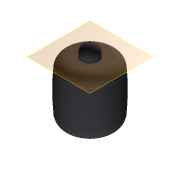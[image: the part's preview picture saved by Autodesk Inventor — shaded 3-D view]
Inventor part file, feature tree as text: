
AUTODESK INVENTOR PART (.ipt)
format: ipt  version: 2017 (Build 210142000, 142)  size: 145,408 bytes
history: native  units: mm
features: sketch x3, fillet x3, mirror x2, plane x1, loft x1, extrude x1
ambient origin geometry x8: Origin, YZ Plane, XZ Plane, XY Plane, X Axis, Y Axis, Z Axis, Center Point
bodies: Solid1 (feature_tree)
feature tree (11):
  sketch  "Sketch1"  dims[d0=12.0mm d1=6.0mm d2=10.5mm d3=0.0mm d4=90.0deg]
  plane  "Work Plane1"
  loft  "Loft1"
  mirror  "Mirror1"
  fillet  "Fillet1"  Radius=10.5mm
  fillet  "Fillet2"  [1 undecoded]
  extrude  "Extrusion1"  Depth=50.0mm
  fillet  "Fillet3"  Radius=2.0mm
  mirror  "Mirror2"
  sketch  "Sketch2"  dims[d5=0.0mm d6=90.0deg d7=50.0mm d8=2.0mm]
  sketch  "Sketch3"  dims[d9=3.5mm d10=2.5mm d11=0.0mm d12=1.75mm]
note: 1 required parameter value undecoded (feature->parameter linkage not recoverable at this tier; creation-order binding heuristic only, values carry confidence <= 0.55)
